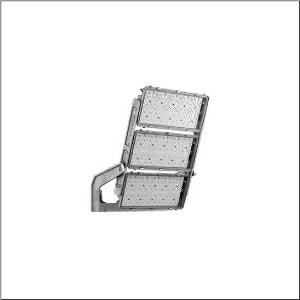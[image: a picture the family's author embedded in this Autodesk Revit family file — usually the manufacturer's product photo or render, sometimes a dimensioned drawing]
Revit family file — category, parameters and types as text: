
# Revit family: floodlight_fl_11_maxi_pro_remote___pl43_5xa779524a01ba_c92a
name_source: partatom
category: Lighting Fixtures
units: mm (PartAtom-declared; Revit-internal decimal feet)

## family parameters
Cut with Voids When Loaded = No
Host = Face
Light Source = No
Part Type = Normal
Room Calculation Point = No
Round Connector Dimension = Use Diameter
Shared = No

## types (1)
- --- (1 x LED, 108940 lm, 1020.5 W, 5700K)
    Apparent Load = 1020 VA
    CIE Flux Codes = 25 74 99 100 100
    Color Rendering = 90
    Color Temperature = 5700K
    Default Elevation = 1800 mm
    Description = Floodlight FL 11  maxi  pro Remote floodlight; light control with lens of PMMA; cover panel of toughened safety glass, transparent; light distribution: PL43, asymmetric direct distribution, LEDcolour temperature: 5700K, rated luminous flux: 108.940lm, colour rendering: CRI > 90, light colour: 957; luminous efficacy: 107lm/W; brightness control: DMX+RDM; with terminal, 8-pole, max. 2.5mm², mains connection: 220..240V/380..400V AC, 50/60Hz, surge voltage resistance: line to ground: 10kV, ECG replaceable separately, LED unit replaceable without ESD environment, dustproof LED module, dimming range 10..100%; 1021W reduction: 440W; floodlight with 3x LED unit of diecast aluminium, coated grey; length: 713mm / width: 651mm / height: 338mm; housing frame, of diecast aluminium, uncoated, natural, mounting bracket, of diecast aluminium, uncoated, natural, equipment: Longlife, protection rating (complete): IP66; insulation class (complete): insulation class I (protective earthing); certification: CE, ENEC, VDE; ball protection: ball impact resistance with accessories, only for outdoor installations, rated ambient temperature 10°C, permissible operating ambient temperature: -40..+40°C, permissible storage temperature: -40..+85°C; packaging unit: 1 piece

Light Distribution: PL43
    Height = 320 mm
    Lamp = 1 x LED
    Lamp Light Flux = 108940 lm
    Lamp Power = 1020.5 W
    Lamp count = 1
    Length = 1002 mm
    Luminous efficacy = 107 lm/W
    Manufacturer = Siteco
    ModVariant = No
    Model = 5XA779524A01BA
    Number of Poles = 1
    OnlyDefault = Yes
    Power Factor = 1
    Product Name = Floodlight FL 11 maxi pro Remote | PL43
    Product group = floodlight | pylon top
    ProductGroupID = 6101
    Protection Class = Protection class I
    Protection Degree = IP 66
    RLX_Detail_Level = 1
    RlxData = <blob elided: 52181 chars, md5=9a3bbe47>
    Socket = socket
    Standby Power = 0 W
    System Light Flux = 108940 lm
    System Power = 1020 W
    Type Comments = factory setting: luminous flux: 100 % | dim-lin: 255 | 710 mA
    Type Image = l_1006784.jpg
    URL = http://relux.com
    VarID = @adj_006119
    Voltage = 0 V
    Weight = 0.00 kg
    Width = 655 mm

## geometry (parser evidence)
native form markers: Blend x4, Sweep x12
no freeform markers — native parametric forms only
